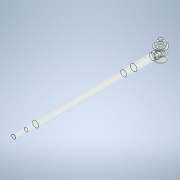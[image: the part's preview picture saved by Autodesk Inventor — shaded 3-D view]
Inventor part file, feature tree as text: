
AUTODESK INVENTOR PART (.ipt)
format: ipt  version: 2020 (Build 240168000, 168)  size: 243,200 bytes
history: native  units: mm
features: sketch x12, extrude x9, revolve x1, plane x1
ambient origin geometry x8: Origin, YZ Plane, XZ Plane, XY Plane, X Axis, Y Axis, Z Axis, Center Point
bodies: Solid1 (feature_tree)
feature tree (23):
  revolve  "Revolution1"  [1 undecoded]
  sketch  "Sketch2"  dims[d2=5.5mm d4=280.0mm]
  extrude  "Extrusion1"  Depth=280.0mm
  extrude  "Extrusion2"  Depth=9.0mm
  extrude  "Extrusion3"  Depth=10.0mm
  extrude  "Extrusion4"  Depth=0.95mm
  extrude  "Extrusion5"  Depth=13.0mm
  extrude  "Extrusion6"  Depth=11.95mm TaperAngle=0.0deg
  extrude  "Extrusion7"  Depth=15.0mm TaperAngle=0.0deg
  extrude  "Extrusion8"  Depth=31.0mm
  sketch  "Sketch11"  dims[d41=2.0mm d42=0.0mm]
  plane  "Work Plane1"
  extrude  "Extrusion9"  Depth=26.0mm
  sketch  "Sketch1"  dims[d0=8.0mm d1=40.0mm]
  sketch  "Sketch3"  dims[d5=9.0mm d8=60.0mm]
  sketch  "Sketch4"  dims[d10=90.0deg d11=10.0mm]
  sketch  "Sketch5"  dims[d21=30.0mm d22=0.95mm]
  sketch  "Sketch6"  dims[d23=24.0mm d24=13.0mm]
  sketch  "Sketch7"  dims[d25=20.0mm d26=11.95mm d27=0.0mm]
  sketch  "Sketch8"  dims[d28=24.0mm d30=20.0mm d31=15.0mm d32=4.0mm d33=0.0mm d34=0.0mm]
  sketch  "Sketch9"  dims[d35=26.0mm d36=31.0mm]
  sketch  "Sketch10"  dims[d37=7.955mm d38=0.0mm d39=26.0mm d40=31.0mm]
  sketch  "Sketch12"  dims[d43=26.0mm d44=31.0mm d45=15.0mm d46=0.0mm d47=12.0mm d48=37.0mm d49=2.0mm d50=0.0mm d51=12.0mm d52=28.0mm d53=8.0mm d54=0.0mm d55=14.0mm d56=11.0mm d57=0.0mm d58=22.0mm d59=10.0mm d60=0.0mm]
note: 1 required parameter value undecoded (feature->parameter linkage not recoverable at this tier; creation-order binding heuristic only, values carry confidence <= 0.55)
